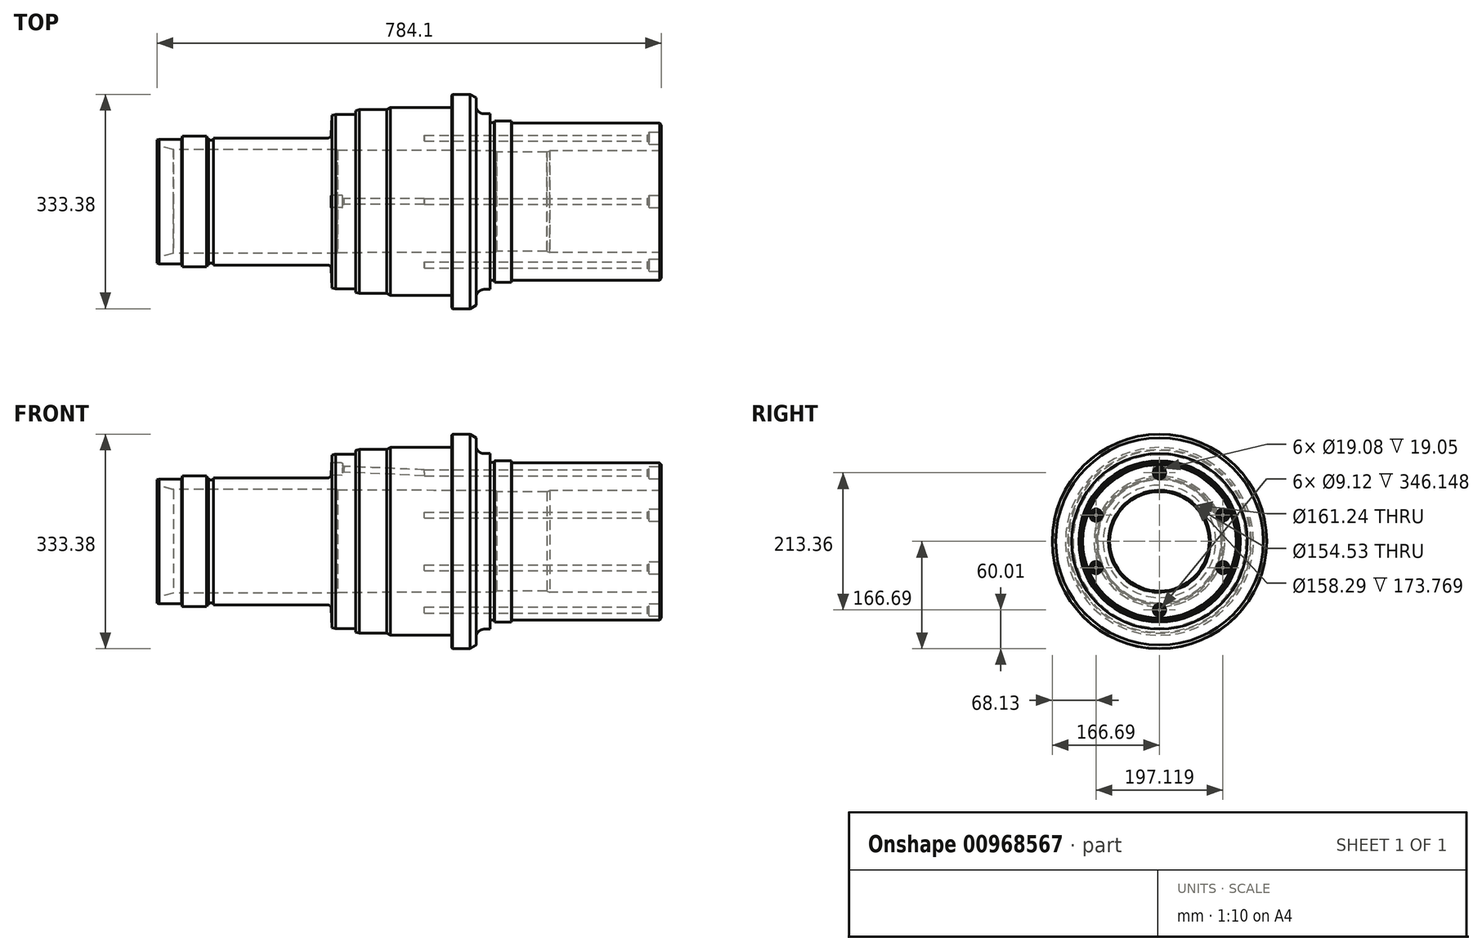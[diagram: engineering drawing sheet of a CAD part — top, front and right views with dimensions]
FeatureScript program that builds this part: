
annotation { "Feature Type Name" : "Feature", "Feature Type Description" : "" }
export const myFeature = defineFeature(function(context is Context, id is Id, definition is map)
    precondition{}
    {
        {
            var Q0;
            Q0=qCreatedBy(makeId("Front.planeOp"),FACE);
            var sketch = newSketch(context, id + "F0", { "sketchPlane" : qUnion([Q0])});
            skLineSegment(sketch, "E0", {"start": v(0, 0) * mm, "end": v(784.1, 0) * mm, "construction": true});
            skLineSegment(sketch, "E1", {"start": v(0, 96.84) * mm, "end": v(38.1, 96.84) * mm});
            skLineSegment(sketch, "E2", {"start": v(25.55, 80.62) * mm, "end": v(279.4, 80.62) * mm});
            skLineSegment(sketch, "E3", {"start": v(39.38, 101.6) * mm, "end": v(77, 101.6) * mm});
            skLineSegment(sketch, "E4", {"start": v(77.72, 98.87) * mm, "end": v(80.16, 98.87) * mm});
            skLineSegment(sketch, "E5", {"start": v(80.16, 98.87) * mm, "end": v(80.16, 95.7) * mm});
            skLineSegment(sketch, "E6", {"start": v(80.16, 95.7) * mm, "end": v(88.09, 95.7) * mm});
            skLineSegment(sketch, "E7", {"start": v(88.09, 95.7) * mm, "end": v(88.09, 98.87) * mm});
            skLineSegment(sketch, "E8", {"start": v(88.09, 98.87) * mm, "end": v(270.59, 98.87) * mm});
            skLineSegment(sketch, "E9", {"start": v(272.2, 135.64) * mm, "end": v(308.69, 135.64) * mm});
            skLineSegment(sketch, "E10", {"start": v(308.69, 135.64) * mm, "end": v(308.69, 142.88) * mm});
            skLineSegment(sketch, "E11", {"start": v(308.69, 142.88) * mm, "end": v(357.2, 142.88) * mm});
            skLineSegment(sketch, "E12", {"start": v(357.2, 142.87) * mm, "end": v(362.7, 146.05) * mm});
            skLineSegment(sketch, "E13", {"start": v(362.7, 146.05) * mm, "end": v(457.99, 146.05) * mm});
            skLineSegment(sketch, "E14", {"start": v(457.99, 146.05) * mm, "end": v(457.99, 166.69) * mm});
            skLineSegment(sketch, "E15", {"start": v(457.99, 166.69) * mm, "end": v(495.94, 166.69) * mm});
            skLineSegment(sketch, "E16", {"start": v(495.94, 166.69) * mm, "end": v(495.94, 136.53) * mm});
            skLineSegment(sketch, "E17", {"start": v(495.94, 136.53) * mm, "end": v(517.52, 136.53) * mm});
            skLineSegment(sketch, "E18", {"start": v(517.52, 136.53) * mm, "end": v(517.52, 122.5) * mm});
            skLineSegment(sketch, "E19", {"start": v(517.52, 122.5) * mm, "end": v(523.88, 122.5) * mm});
            skLineSegment(sketch, "E20", {"start": v(523.88, 122.5) * mm, "end": v(524.65, 125.41) * mm});
            skLineSegment(sketch, "E21", {"start": v(524.65, 125.41) * mm, "end": v(550.85, 125.41) * mm});
            skLineSegment(sketch, "E22", {"start": v(550.85, 125.41) * mm, "end": v(551.7, 122.24) * mm});
            skLineSegment(sketch, "E23", {"start": v(551.7, 122.24) * mm, "end": v(784.1, 122.24) * mm});
            skLineSegment(sketch, "E24", {"start": v(784.1, 79.15) * mm, "end": v(784.1, 122.24) * mm});
            skLineSegment(sketch, "E25", {"start": v(784.1, 79.15) * mm, "end": v(610.33, 79.15) * mm});
            skLineSegment(sketch, "E26", {"start": v(610.33, 79.15) * mm, "end": v(606.3, 77.27) * mm});
            skLineSegment(sketch, "E27", {"start": v(606.3, 77.27) * mm, "end": v(527.92, 77.27) * mm});
            skLineSegment(sketch, "E28", {"start": v(279.4, 80.62) * mm, "end": v(281.23, 79.57) * mm});
            skLineSegment(sketch, "E29", {"start": v(281.23, 79.57) * mm, "end": v(526.04, 79.15) * mm});
            skLineSegment(sketch, "E30", {"start": v(527.92, 77.27) * mm, "end": v(526.04, 79.15) * mm});
            skLineSegment(sketch, "E31", {"start": v(270.59, 98.87) * mm, "end": v(272.2, 135.64) * mm});
            skLineSegment(sketch, "E32", {"start": v(38.1, 96.84) * mm, "end": v(39.38, 101.6) * mm});
            skLineSegment(sketch, "E33", {"start": v(77.72, 98.87) * mm, "end": v(77, 101.6) * mm});
            skPoint(sketch, "E34.end.orphan", {"position": v(38.1, 101.6) * mm});
            skLineSegment(sketch, "E35", {"start": v(0, 87.46) * mm, "end": v(25.55, 80.62) * mm});
            skLineSegment(sketch, "E36", {"start": v(0, 96.84) * mm, "end": v(0, 87.46) * mm});
            skSolve(sketch);
        }
        {
            var Q0;
            Q0=qSketchRegion(id+"F0",true);
            var Q1;
            Q1=sQuery(id+"F0.wireOp",EDGE,"E0");
            revolve(context, id + "F1", {"surfaceOperationType" : NewSurfaceOperationType.NEW, "entities" : qUnion([Q0]), "axis" : qUnion([Q1]), "revolveType" : RevolveType.FULL});
        }
        {
            var Q0;
            Q0=makeQuery(id+"F1.opRevolve","SWEPT_EDGE",EDGE,{"disambiguationData":[OSD([sQuery(id+"F0.wireOp",EDGE,"E15"),sQuery(id+"F0.wireOp",EDGE,"E16")])]});
            chamfer(context, id + "F2", {"entities" : qUnion([Q0]), "chamferType" : ChamferType.OFFSET_ANGLE, "width" : 9.52 * mm, "oppositeDirection" : false, "angle" : 30 * degree, "tangentPropagation" : true});
        }
        {
            var Q0;
            Q0=makeQuery(id+"F1.opRevolve","SWEPT_EDGE",EDGE,{"disambiguationData":[OSD([sQuery(id+"F0.wireOp",EDGE,"E16"),sQuery(id+"F0.wireOp",EDGE,"E17")])]});
            fillet(context, id + "F3", {"entities" : qUnion([Q0]), "radius" : 12.7 * mm, "tangentPropagation" : true, "allowEdgeOverflow" : false});
        }
        {
            var Q0;
            Q0=makeQuery(id+"F1.opRevolve","SWEPT_EDGE",EDGE,{"disambiguationData":[OSD([sQuery(id+"F0.wireOp",EDGE,"E8"),sQuery(id+"F0.wireOp",EDGE,"E31")])]});
            fillet(context, id + "F4", {"entities" : qUnion([Q0]), "radius" : 5.08 * mm, "tangentPropagation" : true, "allowEdgeOverflow" : false});
        }
        {
            var Q0;
            Q0=makeQuery(id+"F1.opRevolve","SWEPT_EDGE",EDGE,{"disambiguationData":[OSD([sQuery(id+"F0.wireOp",EDGE,"E9"),sQuery(id+"F0.wireOp",EDGE,"E31")])]});
            var Q1;
            Q1=makeQuery(id+"F1.opRevolve","SWEPT_EDGE",EDGE,{"disambiguationData":[OSD([sQuery(id+"F0.wireOp",EDGE,"E10"),sQuery(id+"F0.wireOp",EDGE,"E11")])]});
            chamfer(context, id + "F5", {"entities" : qUnion([Q0, Q1]), "chamferType" : ChamferType.OFFSET_ANGLE, "width" : 1.27 * mm, "oppositeDirection" : false, "angle" : 75 * degree, "tangentPropagation" : true});
        }
        {
            var Q0;
            Q0=makeQuery(id+"F1.opRevolve","SWEPT_EDGE",EDGE,{"disambiguationData":[OSD([sQuery(id+"F0.wireOp",EDGE,"E1"),sQuery(id+"F0.wireOp",EDGE,"SCYpA8kQ-7sTV-xUNJ-m1pp-K6qHX3d4gstn")])]});
            chamfer(context, id + "F6", {"entities" : qUnion([Q0]), "chamferType" : ChamferType.OFFSET_ANGLE, "width" : 0.86 * mm, "oppositeDirection" : false, "angle" : 75 * degree, "tangentPropagation" : true});
        }
        {
            var Q0;
            Q0=makeQuery(id+"F1.opRevolve","SWEPT_EDGE",EDGE,{"disambiguationData":[OSD([sQuery(id+"F0.wireOp",EDGE,"E23"),sQuery(id+"F0.wireOp",EDGE,"E24")])]});
            chamfer(context, id + "F7", {"entities" : qUnion([Q0]), "width" : 3.05 * mm, "tangentPropagation" : true});
        }
        {
            var Q0;
            Q0=makeQuery(id+"F1.opRevolve","SWEPT_EDGE",EDGE,{"disambiguationData":[OSD([sQuery(id+"F0.wireOp",EDGE,"E14"),sQuery(id+"F0.wireOp",EDGE,"E15")])]});
            chamfer(context, id + "F8", {"entities" : qUnion([Q0]), "width" : 1.52 * mm, "tangentPropagation" : true});
        }
        {
            var Q0;
            Q0=makeQuery(id+"F1.opRevolve","SWEPT_FACE",FACE,{"disambiguationData":[OSD([sQuery(id+"F0.wireOp",EDGE,"E24")])]});
            var sketch = newSketch(context, id + "F9", { "sketchPlane" : qUnion([Q0])});
            skCircle(sketch, "E37", {"center": v(0, 106.68) * mm, "radius": 4.56 * mm});
            skCircle(sketch, "E38", {"center": v(0, -106.68) * mm, "radius": 4.56 * mm});
            skCircle(sketch, "E39", {"center": v(98.52, 40.92) * mm, "radius": 4.56 * mm});
            skCircle(sketch, "E40", {"center": v(98.56, -40.82) * mm, "radius": 4.56 * mm});
            skCircle(sketch, "E41", {"center": v(-98.56, -40.82) * mm, "radius": 4.56 * mm});
            skCircle(sketch, "E42", {"center": v(-98.56, 40.83) * mm, "radius": 4.56 * mm});
            skLineSegment(sketch, "E43", {"start": v(-107.72, 0) * mm, "end": v(113.39, 0) * mm, "construction": true});
            skLineSegment(sketch, "E44", {"start": v(0, 0) * mm, "end": v(98.52, 40.92) * mm, "construction": true});
            skLineSegment(sketch, "E45", {"start": v(0, 0) * mm, "end": v(-98.56, 40.83) * mm, "construction": true});
            skLineSegment(sketch, "E46", {"start": v(0, 0) * mm, "end": v(-98.56, -40.82) * mm, "construction": true});
            skLineSegment(sketch, "E47", {"start": v(0, 0) * mm, "end": v(98.56, -40.82) * mm, "construction": true});
            skSolve(sketch);
        }
        {
            var Q0;
            Q0=qSketchRegion(id+"F9",true);
            extrude(context, id + "F10", {"entities" : qUnion([Q0]), "operationType" : NewBodyOperationType.REMOVE, "oppositeDirection" : true, "depth" : 368.3 * mm, "offsetDistance" : 25.4 * mm});
        }
        {
            var Q0;
            Q0=makeQuery(id+"F1.opRevolve","SWEPT_FACE",FACE,{"disambiguationData":[OSD([sQuery(id+"F0.wireOp",EDGE,"E24")])]});
            var sketch = newSketch(context, id + "F11", { "sketchPlane" : qUnion([Q0])});
            skCircle(sketch, "E48", {"center": v(98.52, 40.92) * mm, "radius": 9.54 * mm});
            skCircle(sketch, "E49", {"center": v(0, 106.68) * mm, "radius": 9.54 * mm});
            skCircle(sketch, "E50", {"center": v(-98.56, 40.83) * mm, "radius": 9.54 * mm});
            skCircle(sketch, "E51", {"center": v(-98.56, -40.82) * mm, "radius": 9.54 * mm});
            skCircle(sketch, "E52", {"center": v(98.56, -40.82) * mm, "radius": 9.54 * mm});
            skCircle(sketch, "E53", {"center": v(0, -106.68) * mm, "radius": 9.54 * mm});
            skSolve(sketch);
        }
        {
            var Q0;
            Q0=qSketchRegion(id+"F11",true);
            extrude(context, id + "F12", {"entities" : qUnion([Q0]), "operationType" : NewBodyOperationType.REMOVE, "oppositeDirection" : true, "depth" : 19.05 * mm, "offsetDistance" : 25.4 * mm});
        }
        {
            var Q0;
            Q0=makeQuery(id+"F12.boolean.opBoolean","INTERSECT",EDGE,{"derivedFrom":[makeQuery(id+"F10.boolean.opBoolean","COPY",FACE,{"derivedFrom":makeQuery(id+"F10.opExtrude","SWEPT_FACE",FACE,{"disambiguationData":[OSD([sQuery(id+"F9.wireOp",EDGE,"E37")])]})}),makeQuery(id+"F12.opExtrude","CAP_FACE",FACE,{"disambiguationData":[OSD([sQuery(id+"F11.wireOp",EDGE,"E49")])],"isStart":false})]});
            var Q1;
            Q1=makeQuery(id+"F12.boolean.opBoolean","INTERSECT",EDGE,{"derivedFrom":[makeQuery(id+"F10.boolean.opBoolean","COPY",FACE,{"derivedFrom":makeQuery(id+"F10.opExtrude","SWEPT_FACE",FACE,{"disambiguationData":[OSD([sQuery(id+"F9.wireOp",EDGE,"E42")])]})}),makeQuery(id+"F12.opExtrude","CAP_FACE",FACE,{"disambiguationData":[OSD([sQuery(id+"F11.wireOp",EDGE,"E50")])],"isStart":false})]});
            var Q2;
            Q2=makeQuery(id+"F12.boolean.opBoolean","INTERSECT",EDGE,{"derivedFrom":[makeQuery(id+"F10.boolean.opBoolean","COPY",FACE,{"derivedFrom":makeQuery(id+"F10.opExtrude","SWEPT_FACE",FACE,{"disambiguationData":[OSD([sQuery(id+"F9.wireOp",EDGE,"E38")])]})}),makeQuery(id+"F12.opExtrude","CAP_FACE",FACE,{"disambiguationData":[OSD([sQuery(id+"F11.wireOp",EDGE,"E53")])],"isStart":false})]});
            var Q3;
            Q3=makeQuery(id+"F12.boolean.opBoolean","INTERSECT",EDGE,{"derivedFrom":[makeQuery(id+"F10.boolean.opBoolean","COPY",FACE,{"derivedFrom":makeQuery(id+"F10.opExtrude","SWEPT_FACE",FACE,{"disambiguationData":[OSD([sQuery(id+"F9.wireOp",EDGE,"E41")])]})}),makeQuery(id+"F12.opExtrude","CAP_FACE",FACE,{"disambiguationData":[OSD([sQuery(id+"F11.wireOp",EDGE,"E51")])],"isStart":false})]});
            var Q4;
            Q4=makeQuery(id+"F12.boolean.opBoolean","INTERSECT",EDGE,{"derivedFrom":[makeQuery(id+"F10.boolean.opBoolean","COPY",FACE,{"derivedFrom":makeQuery(id+"F10.opExtrude","SWEPT_FACE",FACE,{"disambiguationData":[OSD([sQuery(id+"F9.wireOp",EDGE,"E40")])]})}),makeQuery(id+"F12.opExtrude","CAP_FACE",FACE,{"disambiguationData":[OSD([sQuery(id+"F11.wireOp",EDGE,"E52")])],"isStart":false})]});
            var Q5;
            Q5=makeQuery(id+"F12.boolean.opBoolean","INTERSECT",EDGE,{"derivedFrom":[makeQuery(id+"F10.boolean.opBoolean","COPY",FACE,{"derivedFrom":makeQuery(id+"F10.opExtrude","SWEPT_FACE",FACE,{"disambiguationData":[OSD([sQuery(id+"F9.wireOp",EDGE,"E39")])]})}),makeQuery(id+"F12.opExtrude","CAP_FACE",FACE,{"disambiguationData":[OSD([sQuery(id+"F11.wireOp",EDGE,"E48")])],"isStart":false})]});
            chamfer(context, id + "F13", {"entities" : qUnion([Q0, Q1, Q2, Q3, Q4, Q5]), "chamferType" : ChamferType.OFFSET_ANGLE, "width" : 1.8 * mm, "oppositeDirection" : false, "angle" : 60 * degree, "tangentPropagation" : true});
        }
        {
            var Q0;
            Q0=qCreatedBy(makeId("Front.planeOp"),FACE);
            var sketch = newSketch(context, id + "F14", { "sketchPlane" : qUnion([Q0])});
            skPoint(sketch, "E54", {"position": v(415.8, 106.68) * mm});
            skLineSegment(sketch, "E55", {"start": v(415.8, 106.68) * mm, "end": v(269.13, 113.08) * mm});
            skLineSegment(sketch, "E56.0", {"start": v(416, 111.23) * mm, "end": v(288.36, 116.8) * mm});
            skLineSegment(sketch, "E57", {"start": v(416, 111.23) * mm, "end": v(415.8, 106.68) * mm});
            skLineSegment(sketch, "E58", {"start": v(269.32, 117.64) * mm, "end": v(269.13, 113.08) * mm});
            skLineSegment(sketch, "E59.0", {"start": v(288.57, 121.77) * mm, "end": v(269.54, 122.6) * mm});
            skPoint(sketch, "E60", {"position": v(288.16, 112.25) * mm});
            skLineSegment(sketch, "E61", {"start": v(288.36, 116.8) * mm, "end": v(288.57, 121.77) * mm});
            skLineSegment(sketch, "E62", {"start": v(269.32, 117.64) * mm, "end": v(269.54, 122.6) * mm});
            skSolve(sketch);
        }
        {
            var Q0;
            Q0 = qSketchRegion(id + "F14", true);
            var Q1;
            Q1=sQuery(id+"F14.wireOp",EDGE,"E55");
            revolve(context, id + "F15", {"operationType" : NewBodyOperationType.REMOVE, "surfaceOperationType" : NewSurfaceOperationType.NEW, "entities" : qUnion([Q0]), "axis" : qUnion([Q1]), "revolveType" : RevolveType.FULL, "oppositeDirection" : true});
        }
        {
            var Q0;
            Q0=makeQuery(id+"F15.boolean.opBoolean","COPY",EDGE,{"derivedFrom":makeQuery(id+"F15.opRevolve","SWEPT_EDGE",EDGE,{"disambiguationData":[OSD([sQuery(id+"F14.wireOp",EDGE,"E56.0"),sQuery(id+"F14.wireOp",EDGE,"E61")])]})});
            chamfer(context, id + "F16", {"entities" : qUnion([Q0]), "chamferType" : ChamferType.OFFSET_ANGLE, "width" : 2.54 * mm, "oppositeDirection" : false, "angle" : 30 * degree, "tangentPropagation" : true});
        }
    });
